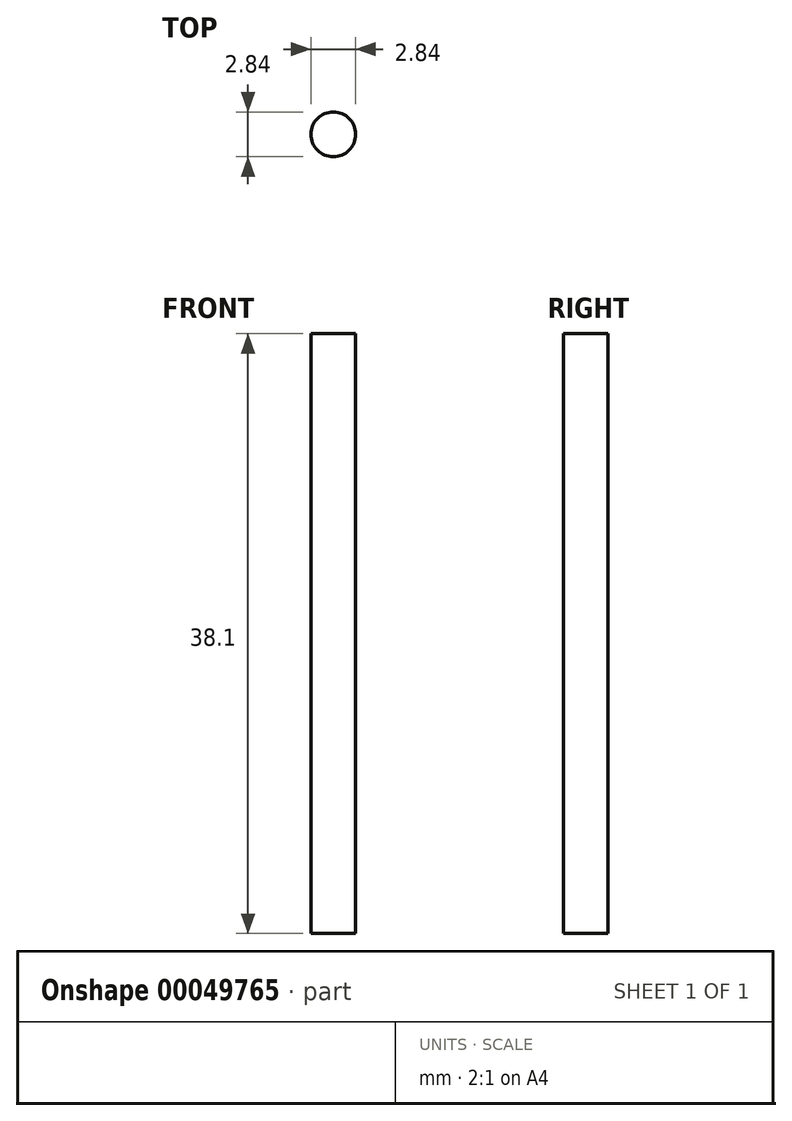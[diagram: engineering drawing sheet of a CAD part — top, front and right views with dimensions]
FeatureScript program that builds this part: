
annotation { "Feature Type Name" : "Feature", "Feature Type Description" : "" }
export const myFeature = defineFeature(function(context is Context, id is Id, definition is map)
    precondition{}
    {
        {
            var Q0;
            Q0=qCreatedBy(makeId("Top.planeOp"),FACE);
            var sketch = newSketch(context, id + "F0", { "sketchPlane" : qUnion([Q0])});
            skCircle(sketch, "E0", {"center": v(0, 0) * mm, "radius": 1.42 * mm});
            skSolve(sketch);
        }
        {
            var Q0;
            Q0 = qSketchRegion(id + "F0", true);
            extrude(context, id + "F1", {"entities" : qUnion([Q0]), "depth" : 38.1 * mm});
        }
    });
